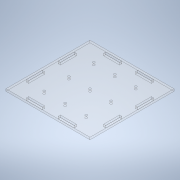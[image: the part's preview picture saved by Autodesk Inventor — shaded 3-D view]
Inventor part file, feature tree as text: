
AUTODESK INVENTOR PART (.ipt)
format: ipt  version: 2021 (Build 250183000, 183)  size: 196,608 bytes
history: native  units: mm
features: sketch x11, hole x9, extrude x2
ambient origin geometry x8: Origin, YZ Plane, XZ Plane, XY Plane, X Axis, Y Axis, Z Axis, Center Point
bodies: Solid1 (feature_tree)
feature tree (22):
  extrude  "Extrusion1"  Depth=106.0mm
  hole  "Hole1"  [1 undecoded]
  extrude  "Extrusion2"  Depth=1.0mm
  hole  "Hole2"  [1 undecoded]
  hole  "Hole3"  [1 undecoded]
  hole  "Hole4"  [1 undecoded]
  hole  "Hole5"  [1 undecoded]
  hole  "Hole6"  [1 undecoded]
  hole  "Hole7"  [1 undecoded]
  hole  "Hole8"  [1 undecoded]
  hole  "Hole9"  [1 undecoded]
  sketch  "Sketch1"  dims[d0=106.0mm d1=106.0mm]
  sketch  "Sketch2"  dims[d4=3.0mm d5=0.0mm d6=1.0mm]
  sketch  "Sketch3"  dims[d7=1.0mm d8=1.0mm]
  sketch  "Sketch5"  dims[d9=1.0mm d10=1.0mm]
  sketch  "Sketch6"  dims[d11=1.0mm d12=1.0mm]
  sketch  "Sketch7"  dims[d13=1.0mm d14=1.0mm]
  sketch  "Sketch8"  dims[d15=3.0mm d16=6.0mm d17=4.0mm d18=2.0mm d19=90.0deg d20=8.0mm d21=20.594885mm d22=112.0mm]
  sketch  "Sketch9"  dims[d23=112.0mm d24=3.0mm d25=0.0mm]
  sketch  "Sketch10"  dims[d26=3.0mm]
  sketch  "Sketch11"  dims[d27=3.0mm d28=6.0mm d29=4.0mm d30=2.0mm d31=90.0deg d32=8.0mm d33=20.594885mm d34=3.0mm]
  sketch  "Sketch12"  dims[d35=3.0mm d36=6.0mm d37=4.0mm d38=2.0mm d39=90.0deg d40=8.0mm d41=20.594885mm d42=3.0mm d43=3.0mm d44=6.0mm d45=4.0mm d46=2.0mm d47=90.0deg d48=8.0mm d49=20.594885mm d50=3.0mm d51=3.0mm d52=6.0mm d53=4.0mm d54=2.0mm d55=90.0deg d56=8.0mm d57=20.594885mm d58=3.0mm d59=3.0mm d60=6.0mm d61=4.0mm d62=2.0mm d63=90.0deg d64=8.0mm d65=20.594885mm d66=3.0mm d67=3.0mm d68=6.0mm d69=4.0mm d70=2.0mm d71=90.0deg d72=8.0mm d73=20.594885mm d74=3.0mm d75=3.0mm d76=6.0mm d77=4.0mm d78=2.0mm d79=90.0deg d80=8.0mm d81=20.594885mm d82=3.0mm d83=3.0mm d84=6.0mm d85=4.0mm d86=2.0mm d87=90.0deg d88=8.0mm d89=20.594885mm]
note: 9 required parameter values undecoded (feature->parameter linkage not recoverable at this tier; creation-order binding heuristic only, values carry confidence <= 0.55)
